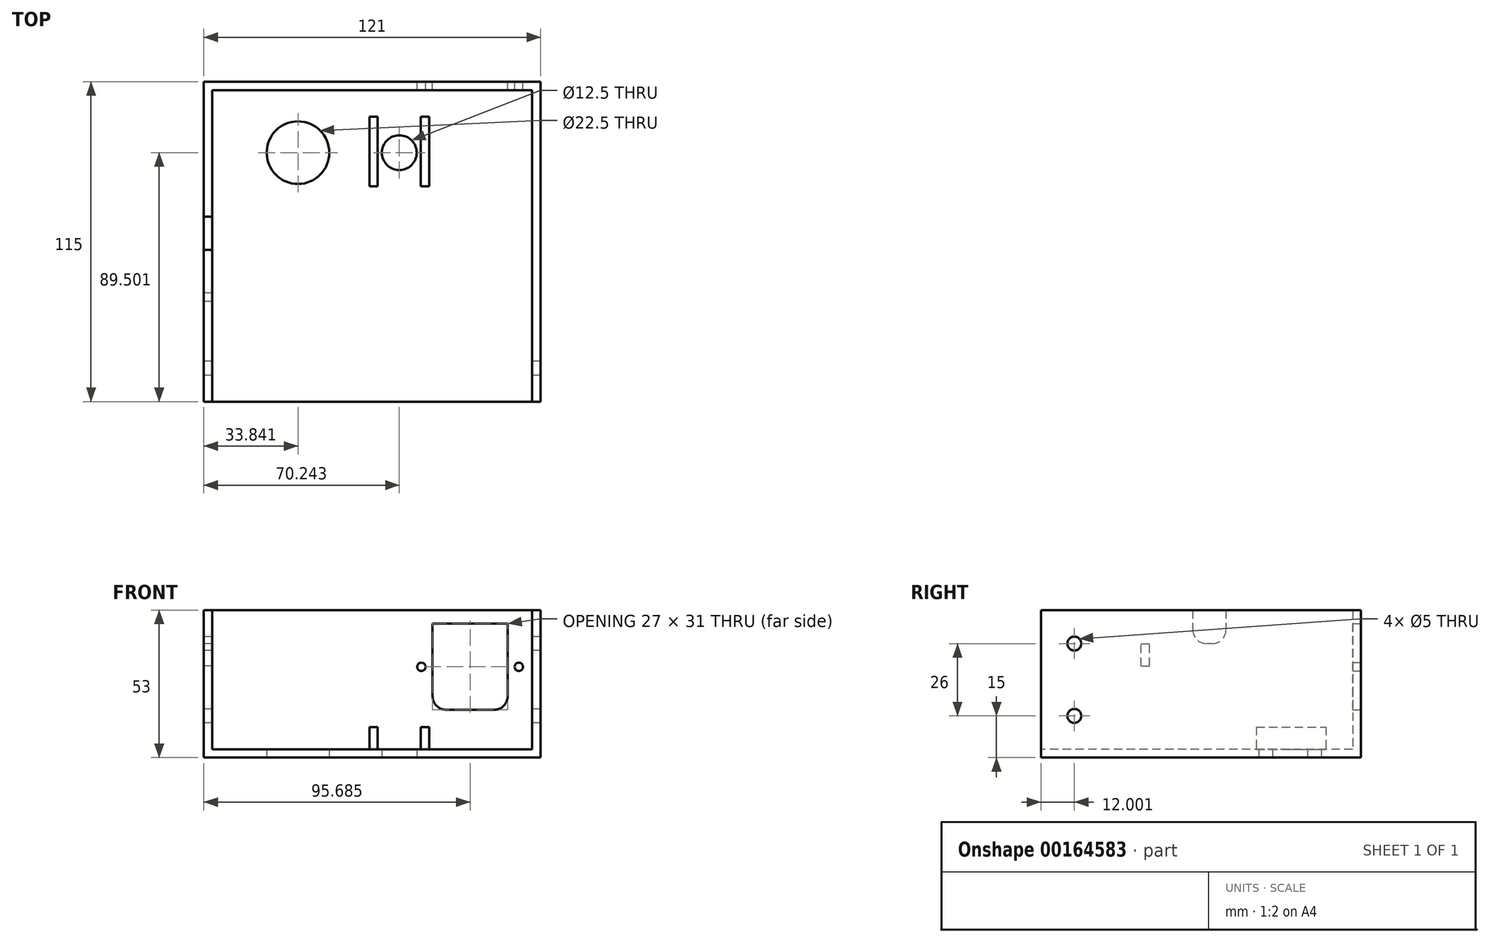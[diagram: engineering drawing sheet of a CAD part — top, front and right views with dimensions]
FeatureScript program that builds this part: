
annotation { "Feature Type Name" : "Feature", "Feature Type Description" : "" }
export const myFeature = defineFeature(function(context is Context, id is Id, definition is map)
    precondition{}
    {
        {
            var Q0;
            Q0=qCreatedBy(makeId("Top.planeOp"),FACE);
            var sketch = newSketch(context, id + "F0", { "sketchPlane" : qUnion([Q0])});
            skLineSegment(sketch, "E0.bottom", {"start": v(-64.55, 79.85) * mm, "end": v(56.45, 79.85) * mm});
            skLineSegment(sketch, "E0.top", {"start": v(-64.55, -35.15) * mm, "end": v(56.45, -35.15) * mm});
            skLineSegment(sketch, "E0.left", {"start": v(-64.55, 79.85) * mm, "end": v(-64.55, -35.15) * mm});
            skLineSegment(sketch, "E0.right", {"start": v(56.45, 79.85) * mm, "end": v(56.45, -35.15) * mm});
            skSolve(sketch);
        }
        {
            var Q0;
            Q0=makeQuery(id+"F0.imprint","IMPRINT",FACE,{"disambiguationData":[TD([[makeQuery(id+"F0.imprint","IMPRINT",EDGE,{"derivedFrom":sQuery(id+"F0.wireOp",EDGE,"E0.bottom")}),-1.0]])]});
            extrude(context, id + "F1", {"entities" : qUnion([Q0]), "depth" : 3 * mm});
        }
        {
            var Q0;
            Q0=makeQuery(id+"F1.opExtrude","CAP_FACE",FACE,{"disambiguationData":[OSD([sQuery(id+"F0.wireOp",EDGE,"E0.bottom"),sQuery(id+"F0.wireOp",EDGE,"E0.top"),sQuery(id+"F0.wireOp",EDGE,"E0.left"),sQuery(id+"F0.wireOp",EDGE,"E0.right")])],"isStart":false});
            var sketch = newSketch(context, id + "F2", { "sketchPlane" : qUnion([Q0])});
            skLineSegment(sketch, "E1.bottom", {"start": v(-64.55, 79.85) * mm, "end": v(56.45, 79.85) * mm});
            skLineSegment(sketch, "E1.top", {"start": v(-64.55, -35.15) * mm, "end": v(56.45, -35.15) * mm});
            skLineSegment(sketch, "E1.left", {"start": v(-64.55, 79.85) * mm, "end": v(-64.55, -35.15) * mm});
            skLineSegment(sketch, "E1.right", {"start": v(56.45, 79.85) * mm, "end": v(56.45, -35.15) * mm});
            skLineSegment(sketch, "E2.bottom", {"start": v(-61.55, 76.85) * mm, "end": v(53.45, 76.85) * mm});
            skLineSegment(sketch, "E2.left", {"start": v(-61.55, 76.85) * mm, "end": v(-61.55, -35.15) * mm});
            skLineSegment(sketch, "E2.right", {"start": v(53.45, 76.85) * mm, "end": v(53.45, -35.15) * mm});
            skSolve(sketch);
        }
        {
            var Q0;
            Q0=makeQuery(id+"F2.imprint","IMPRINT",FACE,{"disambiguationData":[TD([[makeQuery(id+"F2.imprint","IMPRINT",EDGE,{"derivedFrom":sQuery(id+"F2.wireOp",EDGE,"E1.bottom")}),-1.0]])]});
            extrude(context, id + "F3", {"entities" : qUnion([Q0]), "operationType" : NewBodyOperationType.ADD, "depth" : 50 * mm});
        }
        {
            var Q0;
            Q0=makeQuery(id+"F3.boolean.opBoolean","MERGE",FACE,{"derivedFrom":[makeQuery(id+"F1.opExtrude","SWEPT_FACE",FACE,{"disambiguationData":[OSD([sQuery(id+"F0.wireOp",EDGE,"E0.left")])]}),makeQuery(id+"F3.opExtrude","SWEPT_FACE",FACE,{"disambiguationData":[OSD([sQuery(id+"F2.wireOp",EDGE,"E1.left")])]})]});
            var sketch = newSketch(context, id + "F4", { "sketchPlane" : qUnion([Q0])});
            skCircle(sketch, "E3", {"center": v(23.15, 15) * mm, "radius": 2.5 * mm});
            skCircle(sketch, "E4", {"center": v(23.15, 41) * mm, "radius": 2.5 * mm});
            skSolve(sketch);
        }
        {
            var Q0;
            Q0 = qSketchRegion(id + "F4", true);
            extrude(context, id + "F5", {"entities" : qUnion([Q0]), "operationType" : NewBodyOperationType.REMOVE, "endBound" : BoundingType.THROUGH_ALL, "oppositeDirection" : true, "depth" : 25 * mm});
        }
        {
            var Q0;
            Q0=makeQuery(id+"F1.opExtrude","CAP_FACE",FACE,{"disambiguationData":[OSD([sQuery(id+"F0.wireOp",EDGE,"E0.bottom"),sQuery(id+"F0.wireOp",EDGE,"E0.top"),sQuery(id+"F0.wireOp",EDGE,"E0.left"),sQuery(id+"F0.wireOp",EDGE,"E0.right")])],"isStart":true});
            var sketch = newSketch(context, id + "F6", { "sketchPlane" : qUnion([Q0])});
            skLineSegment(sketch, "E5", {"start": v(-64.55, 3.15) * mm, "end": v(56.45, 3.15) * mm, "construction": true});
            skCircle(sketch, "E6", {"center": v(-30.7, -54.35) * mm, "radius": 11.25 * mm});
            skCircle(sketch, "E7", {"center": v(5.7, -54.35) * mm, "radius": 6.25 * mm});
            skLineSegment(sketch, "E8", {"start": v(-64.55, -54.35) * mm, "end": v(35.6, -54.35) * mm, "construction": true});
            skSolve(sketch);
        }
        {
            var Q0;
            Q0 = qSketchRegion(id + "F6", true);
            extrude(context, id + "F7", {"entities" : qUnion([Q0]), "operationType" : NewBodyOperationType.REMOVE, "oppositeDirection" : true, "depth" : 25 * mm});
        }
        {
            var Q0;
            Q0=makeQuery(id+"F1.opExtrude","CAP_FACE",FACE,{"disambiguationData":[OSD([sQuery(id+"F0.wireOp",EDGE,"E0.bottom"),sQuery(id+"F0.wireOp",EDGE,"E0.top"),sQuery(id+"F0.wireOp",EDGE,"E0.left"),sQuery(id+"F0.wireOp",EDGE,"E0.right")])],"isStart":false});
            var sketch = newSketch(context, id + "F8", { "sketchPlane" : qUnion([Q0])});
            skPoint(sketch, "E9", {"position": v(5.7, 54.35) * mm});
            skLineSegment(sketch, "E10.bottom", {"start": v(13.44, 42.23) * mm, "end": v(-2.06, 42.23) * mm});
            skLineSegment(sketch, "E10.top", {"start": v(13.44, 67.23) * mm, "end": v(-2.06, 67.23) * mm});
            skLineSegment(sketch, "E10.left", {"start": v(13.44, 42.23) * mm, "end": v(13.44, 67.23) * mm});
            skLineSegment(sketch, "E10.right", {"start": v(-2.06, 42.23) * mm, "end": v(-2.06, 67.23) * mm});
            skLineSegment(sketch, "E11.bottom", {"start": v(-2.06, 42.23) * mm, "end": v(-5.06, 42.23) * mm});
            skLineSegment(sketch, "E11.top", {"start": v(-2.06, 67.23) * mm, "end": v(-5.06, 67.23) * mm});
            skLineSegment(sketch, "E11.right", {"start": v(-5.06, 42.23) * mm, "end": v(-5.06, 67.23) * mm});
            skLineSegment(sketch, "E12.bottom", {"start": v(13.44, 67.23) * mm, "end": v(16.44, 67.23) * mm});
            skLineSegment(sketch, "E12.top", {"start": v(13.44, 42.23) * mm, "end": v(16.44, 42.23) * mm});
            skLineSegment(sketch, "E12.left", {"start": v(13.44, 67.23) * mm, "end": v(13.44, 42.23) * mm});
            skLineSegment(sketch, "E12.right", {"start": v(16.44, 67.23) * mm, "end": v(16.44, 42.23) * mm});
            skSolve(sketch);
        }
        {
            var Q0;
            Q0=makeQuery(id+"F8.imprint","IMPRINT",FACE,{"disambiguationData":[TD([[makeQuery(id+"F8.imprint","IMPRINT",EDGE,{"derivedFrom":sQuery(id+"F8.wireOp",EDGE,"E11.bottom")}),-1.0]])]});
            var Q1;
            Q1=makeQuery(id+"F8.imprint","IMPRINT",FACE,{"disambiguationData":[TD([[makeQuery(id+"F8.imprint","IMPRINT",EDGE,{"derivedFrom":sQuery(id+"F8.wireOp",EDGE,"E12.bottom")}),-1.0]])]});
            extrude(context, id + "F9", {"entities" : qUnion([Q0, Q1]), "operationType" : NewBodyOperationType.ADD, "depth" : 8 * mm});
        }
        {
            var Q0;
            Q0=makeQuery(id+"F3.boolean.opBoolean","MERGE",FACE,{"derivedFrom":[makeQuery(id+"F1.opExtrude","SWEPT_FACE",FACE,{"disambiguationData":[OSD([sQuery(id+"F0.wireOp",EDGE,"E0.bottom")])]}),makeQuery(id+"F3.opExtrude","SWEPT_FACE",FACE,{"disambiguationData":[OSD([sQuery(id+"F2.wireOp",EDGE,"E1.bottom")])]})]});
            var sketch = newSketch(context, id + "F10", { "sketchPlane" : qUnion([Q0])});
            skLineSegment(sketch, "E13.bottom", {"start": v(-39.63, 17.15) * mm, "end": v(-22.63, 17.15) * mm});
            skLineSegment(sketch, "E13.top", {"start": v(-44.63, 48.15) * mm, "end": v(-17.63, 48.15) * mm});
            skLineSegment(sketch, "E13.left", {"start": v(-44.63, 22.15) * mm, "end": v(-44.63, 48.15) * mm});
            skLineSegment(sketch, "E13.right", {"start": v(-17.63, 22.15) * mm, "end": v(-17.63, 48.15) * mm});
            skPoint(sketch, "E14.visualSharp", {"position": v(-17.63, 17.15) * mm});
            skArc(sketch, "E14.filletArc", {"start": v(-22.63, 17.15) * mm, "mid": v(-19.1, 18.62) * mm, "end": v(-17.63, 22.15) * mm});
            skPoint(sketch, "E15.visualSharp", {"position": v(-44.63, 17.15) * mm});
            skArc(sketch, "E15.filletArc", {"start": v(-44.63, 22.15) * mm, "mid": v(-43.17, 18.62) * mm, "end": v(-39.63, 17.15) * mm});
            skCircle(sketch, "E16", {"center": v(-13.63, 32.65) * mm, "radius": 1.5 * mm});
            skCircle(sketch, "E17", {"center": v(-48.63, 32.65) * mm, "radius": 1.5 * mm});
            skSolve(sketch);
        }
        {
            var Q0;
            Q0 = qSketchRegion(id + "F10", true);
            extrude(context, id + "F11", {"entities" : qUnion([Q0]), "operationType" : NewBodyOperationType.REMOVE, "oppositeDirection" : true, "depth" : 25 * mm});
        }
        {
            var Q0;
            Q0=makeQuery(id+"F3.boolean.opBoolean","MERGE",FACE,{"derivedFrom":[makeQuery(id+"F1.opExtrude","SWEPT_FACE",FACE,{"disambiguationData":[OSD([sQuery(id+"F0.wireOp",EDGE,"E0.left")])]}),makeQuery(id+"F3.opExtrude","SWEPT_FACE",FACE,{"disambiguationData":[OSD([sQuery(id+"F2.wireOp",EDGE,"E1.left")])]})]});
            var sketch = newSketch(context, id + "F12", { "sketchPlane" : qUnion([Q0])});
            skLineSegment(sketch, "E18.bottom", {"start": v(-31.35, 62) * mm, "end": v(-19.35, 62) * mm});
            skLineSegment(sketch, "E18.top", {"start": v(-26.35, 41) * mm, "end": v(-24.35, 41) * mm});
            skLineSegment(sketch, "E18.left", {"start": v(-31.35, 62) * mm, "end": v(-31.35, 46) * mm});
            skLineSegment(sketch, "E18.right", {"start": v(-19.35, 62) * mm, "end": v(-19.35, 46) * mm});
            skPoint(sketch, "E19.visualSharp", {"position": v(-31.35, 41) * mm});
            skArc(sketch, "E19.filletArc", {"start": v(-31.35, 46) * mm, "mid": v(-29.89, 42.46) * mm, "end": v(-26.35, 41) * mm});
            skPoint(sketch, "E20.visualSharp", {"position": v(-19.35, 41) * mm});
            skArc(sketch, "E20.filletArc", {"start": v(-24.35, 41) * mm, "mid": v(-20.82, 42.46) * mm, "end": v(-19.35, 46) * mm});
            skSolve(sketch);
        }
        {
            var Q0;
            Q0 = qSketchRegion(id + "F12", true);
            extrude(context, id + "F13", {"entities" : qUnion([Q0]), "operationType" : NewBodyOperationType.REMOVE, "oppositeDirection" : true, "depth" : 25 * mm});
        }
        {
            var Q0;
            Q0=makeQuery(id+"F12.imprint","IMPRINT",FACE,{"disambiguationData":[TD([[makeQuery(id+"F12.imprint","IMPRINT",EDGE,{"derivedFrom":sQuery(id+"F12.wireOp",EDGE,"E18.top")}),-1.0]])]});
            var sketch = newSketch(context, id + "F14", { "sketchPlane" : qUnion([Q0])});
            skCircle(sketch, "E21.0", {"center": v(23.15, 41) * mm, "radius": 2.5 * mm});
            skLineSegment(sketch, "E22.bottom", {"start": v(-0.85, 33) * mm, "end": v(-3.85, 33) * mm});
            skLineSegment(sketch, "E22.top", {"start": v(-0.85, 41) * mm, "end": v(-3.85, 41) * mm});
            skLineSegment(sketch, "E22.left", {"start": v(-0.85, 33) * mm, "end": v(-0.85, 41) * mm});
            skLineSegment(sketch, "E22.right", {"start": v(-3.85, 33) * mm, "end": v(-3.85, 41) * mm});
            skSolve(sketch);
        }
        {
            var Q0;
            Q0 = qSketchRegion(id + "F14", true);
            extrude(context, id + "F15", {"entities" : qUnion([Q0]), "operationType" : NewBodyOperationType.REMOVE, "oppositeDirection" : true, "depth" : 25 * mm});
        }
    });
